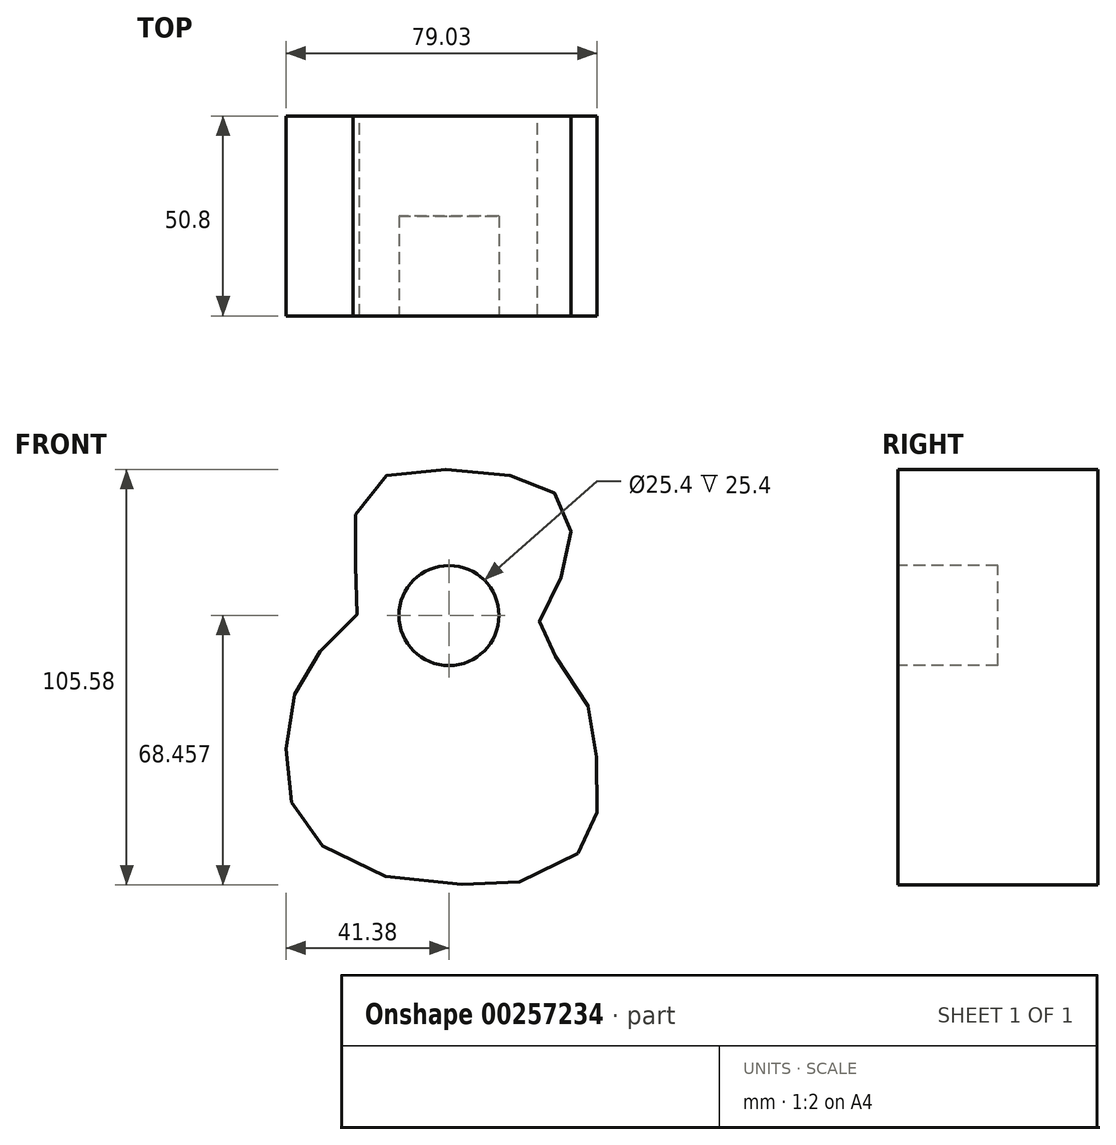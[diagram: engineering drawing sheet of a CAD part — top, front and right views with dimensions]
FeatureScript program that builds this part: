
annotation { "Feature Type Name" : "Feature", "Feature Type Description" : "" }
export const myFeature = defineFeature(function(context is Context, id is Id, definition is map)
    precondition{}
    {
        {
            var Q0;
            Q0=qCreatedBy(makeId("Front.planeOp"),FACE);
            var sketch = newSketch(context, id + "F0", { "sketchPlane" : qUnion([Q0])});
            skFitSpline(sketch, "E0", {"points": [v(-38.61, 11.94) * mm, v(-30.43, 18.82) * mm, v(-28.8, 29.29) * mm, v(-30.1, 36.49) * mm, v(-29.45, 47.29) * mm, v(-24.22, 55.47) * mm, v(-12.1, 58.08) * mm, v(2.62, 57.76) * mm, v(16.69, 54.81) * mm, v(21.6, 51.54) * mm, v(24.87, 45.65) * mm, v(24.22, 37.14) * mm, v(21.93, 29.29) * mm, v(17.67, 21.1) * mm, v(17.02, 14.89) * mm, v(22.9, 9) * mm, v(29.78, -2.78) * mm, v(31.41, -11.94) * mm, v(31.74, -26.34) * mm, v(31.41, -31.25) * mm, v(26.5, -39.76) * mm, v(11.78, -46.63) * mm, v(0, -47.29) * mm, v(-21.6, -45.32) * mm, v(-38.29, -37.14) * mm, v(-45.16, -28.3) * mm, v(-47.12, -18.16) * mm, v(-46.8, -6.38) * mm, v(-43.85, 4.42) * mm, v(-38.61, 11.94) * mm]});
            skSolve(sketch);
        }
        {
            var Q0;
            Q0=makeQuery(id+"F0.imprint","IMPRINT",FACE,{"disambiguationData":[TD([[makeQuery(id+"F0.imprint","IMPRINT",EDGE,{"derivedFrom":sQuery(id+"F0.wireOp",EDGE,"E0")}),-1.0]])]});
            extrude(context, id + "F1", {"entities" : qUnion([Q0]), "depth" : 50.8 * mm});
        }
        {
            var Q0;
            Q0=makeQuery(id+"F1.opExtrude","CAP_FACE",FACE,{"disambiguationData":[OSD([sQuery(id+"F0.wireOp",EDGE,"E0")])],"isStart":false});
            var sketch = newSketch(context, id + "F2", { "sketchPlane" : qUnion([Q0])});
            skCircle(sketch, "E1", {"center": v(-5.9, 21.1) * mm, "radius": 12.7 * mm});
            skSolve(sketch);
        }
        {
            var Q0;
            Q0=makeQuery(id+"F2.imprint","IMPRINT",FACE,{"disambiguationData":[TD([[makeQuery(id+"F2.imprint","IMPRINT",EDGE,{"derivedFrom":sQuery(id+"F2.wireOp",EDGE,"E1")}),1.0]])]});
            extrude(context, id + "F3", {"entities" : qUnion([Q0]), "operationType" : NewBodyOperationType.REMOVE, "oppositeDirection" : true, "depth" : 25.4 * mm});
        }
    });
